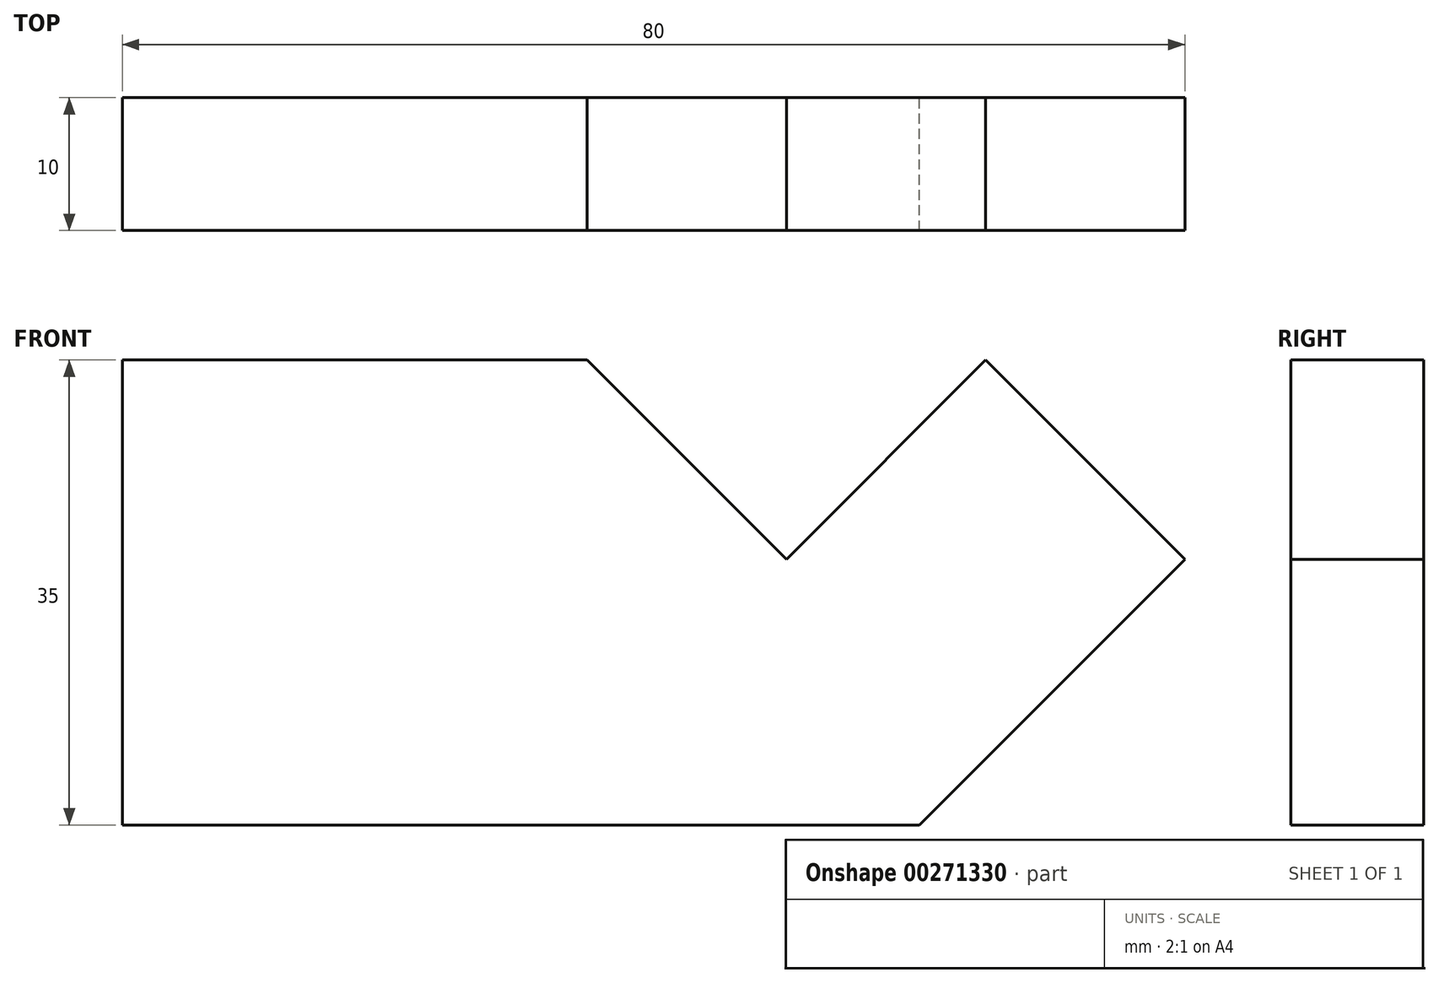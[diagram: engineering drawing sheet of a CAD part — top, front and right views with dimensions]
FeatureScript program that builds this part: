
annotation { "Feature Type Name" : "Feature", "Feature Type Description" : "" }
export const myFeature = defineFeature(function(context is Context, id is Id, definition is map)
    precondition{}
    {
        {
            var Q0;
            Q0=qCreatedBy(makeId("Front.planeOp"),FACE);
            var sketch = newSketch(context, id + "F0", { "sketchPlane" : qUnion([Q0])});
            skLineSegment(sketch, "E0", {"start": v(0, 0) * mm, "end": v(0, 35) * mm});
            skLineSegment(sketch, "E1", {"start": v(0, 0) * mm, "end": v(60, 0) * mm});
            skLineSegment(sketch, "E2", {"start": v(60, 0) * mm, "end": v(80, 20) * mm});
            skLineSegment(sketch, "E3", {"start": v(0, 35) * mm, "end": v(35, 35) * mm});
            skLineSegment(sketch, "E4", {"start": v(35, 35) * mm, "end": v(50, 20) * mm});
            skLineSegment(sketch, "E5", {"start": v(50, 20) * mm, "end": v(65, 35) * mm});
            skLineSegment(sketch, "E6", {"start": v(65, 35) * mm, "end": v(80, 20) * mm});
            skSolve(sketch);
        }
        {
            var Q0;
            Q0=makeQuery(id+"F0.imprint","IMPRINT",FACE,{"disambiguationData":[TD([[makeQuery(id+"F0.imprint","IMPRINT",EDGE,{"derivedFrom":sQuery(id+"F0.wireOp",EDGE,"E0")}),-1.0]])]});
            extrude(context, id + "F1", {"entities" : qUnion([Q0]), "depth" : 10 * mm});
        }
    });
